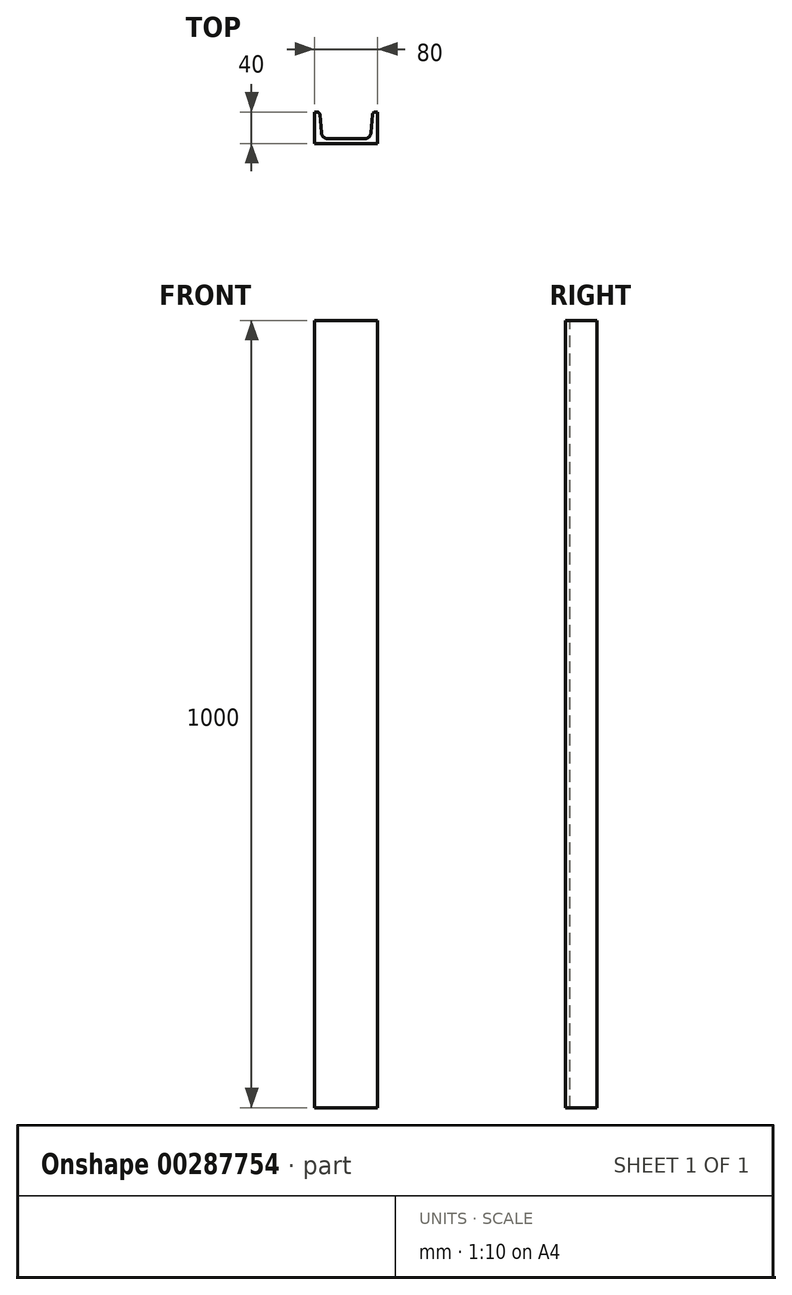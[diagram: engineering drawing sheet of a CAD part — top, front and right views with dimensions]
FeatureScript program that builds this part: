
annotation { "Feature Type Name" : "Feature", "Feature Type Description" : "" }
export const myFeature = defineFeature(function(context is Context, id is Id, definition is map)
    precondition{}
    {
        {
            var Q0;
            Q0=qCreatedBy(makeId("Top.planeOp"),FACE);
            var sketch = newSketch(context, id + "F0", { "sketchPlane" : qUnion([Q0])});
            skLineSegment(sketch, "E0.bottom", {"start": v(-40, -20) * mm, "end": v(40, -20) * mm});
            skLineSegment(sketch, "E0.top", {"start": v(-40, 20) * mm, "end": v(-33.6, 20) * mm});
            skLineSegment(sketch, "E0.left", {"start": v(-40, -20) * mm, "end": v(-40, 20) * mm});
            skLineSegment(sketch, "E0.right", {"start": v(40, -20) * mm, "end": v(40, 20) * mm});
            skLineSegment(sketch, "E1.0", {"start": v(-30.88, -14) * mm, "end": v(30.88, -14) * mm});
            skLineSegment(sketch, "E2.trimOffspring", {"start": v(33.6, 20) * mm, "end": v(40, 20) * mm});
            skLineSegment(sketch, "E3", {"start": v(-33.6, 20) * mm, "end": v(-30.88, -14) * mm});
            skLineSegment(sketch, "E4", {"start": v(33.6, 20) * mm, "end": v(30.88, -14) * mm});
            skPoint(sketch, "E5", {"position": v(-32, 0) * mm});
            skPoint(sketch, "E6", {"position": v(32, 0) * mm});
            skPoint(sketch, "E7", {"position": v(0, -14) * mm});
            skSolve(sketch);
        }
        {
            var Q0;
            Q0=makeQuery(id+"F0.imprint","IMPRINT",FACE,{"disambiguationData":[TD([[makeQuery(id+"F0.imprint","IMPRINT",EDGE,{"derivedFrom":sQuery(id+"F0.wireOp",EDGE,"E0.bottom")}),1.0]])]});
            extrude(context, id + "F1", {"entities" : qUnion([Q0]), "oppositeDirection" : true, "depth" : 1000 * mm});
        }
        {
            var Q0;
            Q0=makeQuery(id+"F1.opExtrude","SWEPT_EDGE",EDGE,{"disambiguationData":[OSD([sQuery(id+"F0.wireOp",EDGE,"E0.top"),sQuery(id+"F0.wireOp",EDGE,"E3")])]});
            var Q1;
            Q1=makeQuery(id+"F1.opExtrude","SWEPT_EDGE",EDGE,{"disambiguationData":[OSD([sQuery(id+"F0.wireOp",EDGE,"E2.trimOffspring"),sQuery(id+"F0.wireOp",EDGE,"E4")])]});
            fillet(context, id + "F2", {"entities" : qUnion([Q0, Q1]), "radius" : 4 * mm, "tangentPropagation" : true, "allowEdgeOverflow" : false});
        }
        {
            var Q0;
            Q0=makeQuery(id+"F1.opExtrude","SWEPT_EDGE",EDGE,{"disambiguationData":[OSD([sQuery(id+"F0.wireOp",EDGE,"E1.0"),sQuery(id+"F0.wireOp",EDGE,"E3")])]});
            var Q1;
            Q1=makeQuery(id+"F1.opExtrude","SWEPT_EDGE",EDGE,{"disambiguationData":[OSD([sQuery(id+"F0.wireOp",EDGE,"E1.0"),sQuery(id+"F0.wireOp",EDGE,"E4")])]});
            fillet(context, id + "F3", {"entities" : qUnion([Q0, Q1]), "radius" : 8 * mm, "tangentPropagation" : true, "allowEdgeOverflow" : false});
        }
    });
